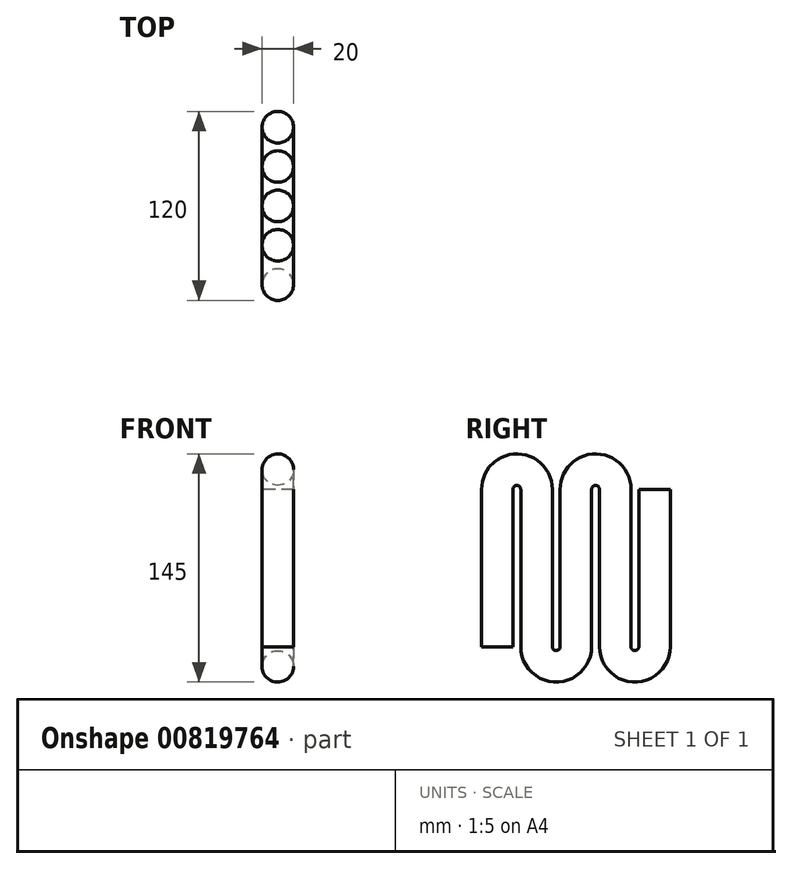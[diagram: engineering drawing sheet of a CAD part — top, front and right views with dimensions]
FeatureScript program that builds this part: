
annotation { "Feature Type Name" : "Feature", "Feature Type Description" : "" }
export const myFeature = defineFeature(function(context is Context, id is Id, definition is map)
    precondition{}
    {
        {
            var Q0;
            Q0=qCreatedBy(makeId("Top.planeOp"),FACE);
            var sketch = newSketch(context, id + "F0", { "sketchPlane" : qUnion([Q0])});
            skCircle(sketch, "E0", {"center": v(0, 0) * mm, "radius": 10 * mm});
            skSolve(sketch);
        }
        {
            var Q0;
            Q0=qCreatedBy(makeId("Right.planeOp"),FACE);
            var sketch = newSketch(context, id + "F1", { "sketchPlane" : qUnion([Q0])});
            skLineSegment(sketch, "E1", {"start": v(0, 0) * mm, "end": v(0, 100) * mm});
            skLineSegment(sketch, "E2", {"start": v(25, 100) * mm, "end": v(25, 0) * mm});
            skLineSegment(sketch, "E3", {"start": v(50, 0) * mm, "end": v(50, 100) * mm});
            skLineSegment(sketch, "E4", {"start": v(75, 100) * mm, "end": v(75, 0) * mm});
            skLineSegment(sketch, "E5", {"start": v(100, 0) * mm, "end": v(100, 100) * mm});
            skArc(sketch, "E6", {"start": v(25, 100) * mm, "mid": v(12.5, 112.5) * mm, "end": v(0, 100) * mm});
            skArc(sketch, "E7", {"start": v(25, 0) * mm, "mid": v(37.5, -12.5) * mm, "end": v(50, 0) * mm});
            skArc(sketch, "E8", {"start": v(75, 100) * mm, "mid": v(62.5, 112.5) * mm, "end": v(50, 100) * mm});
            skArc(sketch, "E9", {"start": v(75, 0) * mm, "mid": v(87.5, -12.5) * mm, "end": v(100, 0) * mm});
            skSolve(sketch);
        }
        {
            var Q0;
            Q0=makeQuery(id+"F0.imprint","IMPRINT",FACE,{"disambiguationData":[TD([[makeQuery(id+"F0.imprint","IMPRINT",EDGE,{"derivedFrom":sQuery(id+"F0.wireOp",EDGE,"E0")}),1.0]])]});
            var Q1;
            Q1 = qConstructionFilter(qBodyType(qCreatedBy(id + "F1" ,EDGE), BodyType.WIRE), ConstructionObject.NO);
            sweep(context, id + "F2", {"profiles" : qUnion([Q0]), "path" : qUnion([Q1])});
        }
    });
